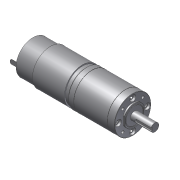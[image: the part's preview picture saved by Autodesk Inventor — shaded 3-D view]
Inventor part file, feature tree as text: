
AUTODESK INVENTOR PART (.ipt)
format: ipt  version: 2012 (Build 160160000, 160)  size: 288,768 bytes
history: native  units: in
note: dims shown in document units (in); Inventor stores cm internally (conversion verified against a paired STEP export)
features: mirror x1, other x1, imported_body x1
ambient origin geometry x8: Origin, YZ Plane, XZ Plane, XY Plane, X Axis, Y Axis, Z Axis, Center Point
feature tree (3):
  mirror  "Mirror2"
  other  "PG-711"
  imported_body  "Base1"
